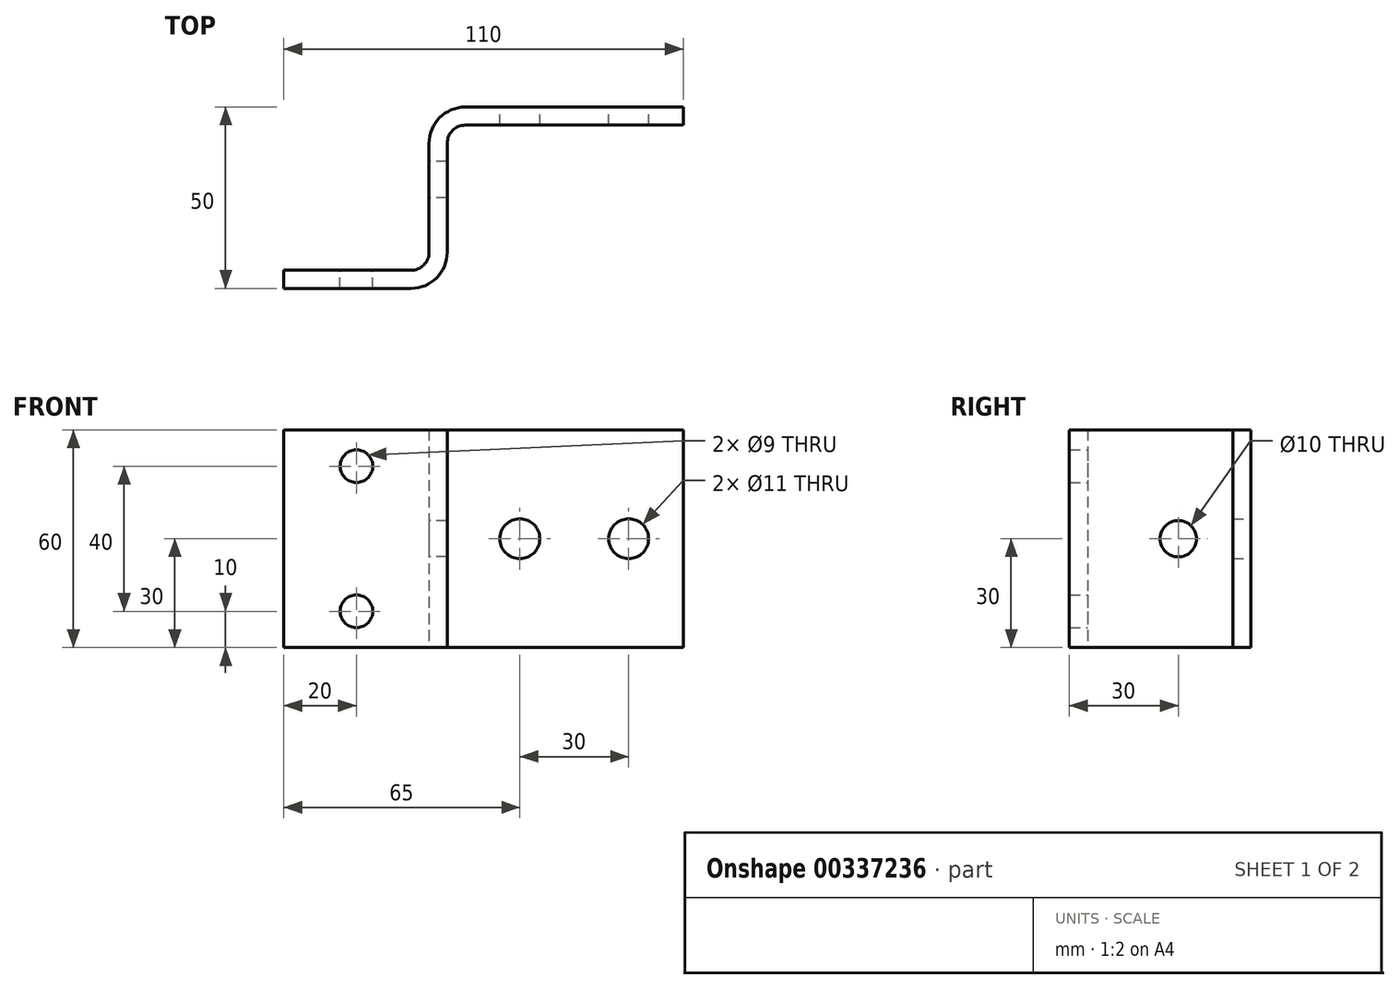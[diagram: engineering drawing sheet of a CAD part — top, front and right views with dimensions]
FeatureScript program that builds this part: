
annotation { "Feature Type Name" : "Feature", "Feature Type Description" : "" }
export const myFeature = defineFeature(function(context is Context, id is Id, definition is map)
    precondition{}
    {
        {
            var Q0;
            Q0=qCreatedBy(makeId("Top.planeOp"),FACE);
            var sketch = newSketch(context, id + "F0", { "sketchPlane" : qUnion([Q0])});
            skLineSegment(sketch, "E0", {"start": v(0, 0) * mm, "end": v(0, 5) * mm});
            skLineSegment(sketch, "E1", {"start": v(0, 5) * mm, "end": v(35, 5) * mm});
            skLineSegment(sketch, "E2", {"start": v(40, 10) * mm, "end": v(40, 40) * mm});
            skLineSegment(sketch, "E3", {"start": v(50, 50) * mm, "end": v(110, 50) * mm});
            skLineSegment(sketch, "E4", {"start": v(110, 50) * mm, "end": v(110, 45) * mm});
            skLineSegment(sketch, "E5", {"start": v(110, 45) * mm, "end": v(50, 45) * mm});
            skLineSegment(sketch, "E6", {"start": v(45, 40) * mm, "end": v(45, 10) * mm});
            skLineSegment(sketch, "E7", {"start": v(35, 0) * mm, "end": v(0, 0) * mm});
            skPoint(sketch, "E8.visualSharp", {"position": v(40, 50) * mm});
            skArc(sketch, "E8.filletArc", {"start": v(50, 50) * mm, "mid": v(42.93, 47.07) * mm, "end": v(40, 40) * mm});
            skPoint(sketch, "E9.visualSharp", {"position": v(45, 0) * mm});
            skArc(sketch, "E9.filletArc", {"start": v(35, 0) * mm, "mid": v(42.07, 2.93) * mm, "end": v(45, 10) * mm});
            skPoint(sketch, "E10.visualSharp", {"position": v(45, 45) * mm});
            skArc(sketch, "E10.filletArc", {"start": v(50, 45) * mm, "mid": v(46.46, 43.54) * mm, "end": v(45, 40) * mm});
            skPoint(sketch, "E11.visualSharp", {"position": v(40, 5) * mm});
            skArc(sketch, "E11.filletArc", {"start": v(35, 5) * mm, "mid": v(38.54, 6.46) * mm, "end": v(40, 10) * mm});
            skSolve(sketch);
        }
        {
            var Q0;
            Q0 = qSketchRegion(id + "F0", true);
            extrude(context, id + "F1", {"entities" : qUnion([Q0]), "depth" : 60 * mm});
        }
        {
            var Q0;
            Q0=makeQuery(id+"F1.opExtrude","SWEPT_FACE",FACE,{"disambiguationData":[OSD([sQuery(id+"F0.wireOp",EDGE,"E1")])]});
            cPlane(context, id + "F2", {"entities" : qUnion([Q0]), "cplaneType" : CPlaneType.OFFSET, "offset" : 0 * mm, "width" : 150 * mm, "height" : 150 * mm});
        }
        {
            var Q0;
            Q0=qCreatedBy(id+"F2.planeOp",FACE);
            var sketch = newSketch(context, id + "F3", { "sketchPlane" : qUnion([Q0])});
            skCircle(sketch, "E12", {"center": v(-20, 10) * mm, "radius": 4.5 * mm});
            skCircle(sketch, "E13", {"center": v(-20, 50) * mm, "radius": 4.5 * mm});
            skSolve(sketch);
        }
        {
            var Q0;
            Q0 = qSketchRegion(id + "F3", true);
            extrude(context, id + "F4", {"entities" : qUnion([Q0]), "operationType" : NewBodyOperationType.REMOVE, "oppositeDirection" : true, "depth" : 25 * mm});
        }
        {
            var Q0;
            Q0=makeQuery(id+"F1.opExtrude","SWEPT_FACE",FACE,{"disambiguationData":[OSD([sQuery(id+"F0.wireOp",EDGE,"E3")])]});
            cPlane(context, id + "F5", {"entities" : qUnion([Q0]), "cplaneType" : CPlaneType.OFFSET, "offset" : 0 * mm, "width" : 150 * mm, "height" : 150 * mm});
        }
        {
            var Q0;
            Q0=qCreatedBy(id+"F5.planeOp",FACE);
            var sketch = newSketch(context, id + "F6", { "sketchPlane" : qUnion([Q0])});
            skCircle(sketch, "E14", {"center": v(-65, 30) * mm, "radius": 5.5 * mm});
            skCircle(sketch, "E15", {"center": v(-95, 30) * mm, "radius": 5.5 * mm});
            skSolve(sketch);
        }
        {
            var Q0;
            Q0 = qSketchRegion(id + "F6", true);
            extrude(context, id + "F7", {"entities" : qUnion([Q0]), "operationType" : NewBodyOperationType.REMOVE, "oppositeDirection" : true, "depth" : 25 * mm});
        }
        {
            var Q0;
            Q0=makeQuery(id+"F1.opExtrude","SWEPT_FACE",FACE,{"disambiguationData":[OSD([sQuery(id+"F0.wireOp",EDGE,"E2")])]});
            cPlane(context, id + "F8", {"entities" : qUnion([Q0]), "cplaneType" : CPlaneType.OFFSET, "offset" : 0 * mm, "width" : 150 * mm, "height" : 150 * mm});
        }
        {
            var Q0;
            Q0=qCreatedBy(id+"F8.planeOp",FACE);
            var sketch = newSketch(context, id + "F9", { "sketchPlane" : qUnion([Q0])});
            skCircle(sketch, "E16", {"center": v(-30, 30) * mm, "radius": 5 * mm});
            skSolve(sketch);
        }
        {
            var Q0;
            Q0 = qSketchRegion(id + "F9", true);
            extrude(context, id + "F10", {"entities" : qUnion([Q0]), "operationType" : NewBodyOperationType.REMOVE, "oppositeDirection" : true, "depth" : 25 * mm});
        }
    });
